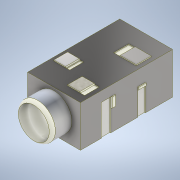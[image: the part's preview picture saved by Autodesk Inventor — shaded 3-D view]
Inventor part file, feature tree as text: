
AUTODESK INVENTOR PART (.ipt)
format: ipt  version: 2020 (Build 240168000, 168)  size: 257,536 bytes
history: native  units: in
note: dims shown in document units (in); Inventor stores cm internally (conversion verified against a paired STEP export)
features: extrude x11, sketch x7, chamfer x3, thread x1, fillet x1
ambient origin geometry x8: Origin, YZ Plane, XZ Plane, XY Plane, X Axis, Y Axis, Z Axis, Center Point
bodies: Solid1 (feature_tree)
feature tree (23):
  extrude  "Extrusion1"  Depth=0.5031in
  extrude  "Extrusion2"  Depth=0.3937in TaperAngle=0.0deg
  extrude  "Extrusion3"  Depth=0.0079in TaperAngle=0.0deg
  thread  "Thread1"  [1 undecoded]
  extrude  "Extrusion4"  Depth=0.0079in TaperAngle=0.0deg
  sketch  "Sketch5"  dims[d16=0.0079in d17=0.0in d18=0.0079in d19=0.0787in d20=45.0deg]
  extrude  "Extrusion5"  Depth=0.0079in TaperAngle=45.0deg
  extrude  "Extrusion6"  Depth=0.0079in TaperAngle=0.0deg
  extrude  "Extrusion7"  Depth=0.0079in TaperAngle=0.0deg
  chamfer  "Chamfer1"  Distance=0.0079in
  sketch  "Sketch6"  dims[d21=0.0079in d22=0.0in d23=0.0079in d24=0.0in]
  extrude  "Extrusion8"  Depth=0.0079in TaperAngle=45.0deg
  extrude  "Extrusion9"  Depth=0.0394in
  chamfer  "Chamfer2"  [1 undecoded]
  sketch  "Sketch7"  dims[d25=0.0079in d26=0.0787in d27=45.0deg d28=0.0079in d29=0.0in d30=0.0079in d31=0.0in d32=0.0079in d33=0.0787in d34=45.0deg d35=0.0394in]
  extrude  "Extrusion10"  [1 undecoded]
  extrude  "Extrusion11"  [1 undecoded]
  chamfer  "Chamfer3"  [1 undecoded]
  fillet  "Fillet1"  [1 undecoded]
  sketch  "Sketch1"  dims[d0=0.878in d1=0.5031in]
  sketch  "Sketch2"  dims[d2=0.3937in d3=0.0in d4=0.1929in d5=0.0in]
  sketch  "Sketch3"  dims[d6=0.9449in d7=0.0in d8=0.9449in d9=0.0in d10=0.0079in d11=0.0in]
  sketch  "Sketch4"  dims[d12=0.0079in d13=0.0in d14=0.0079in d15=0.0in]
note: 6 required parameter values undecoded (feature->parameter linkage not recoverable at this tier; creation-order binding heuristic only, values carry confidence <= 0.55)
